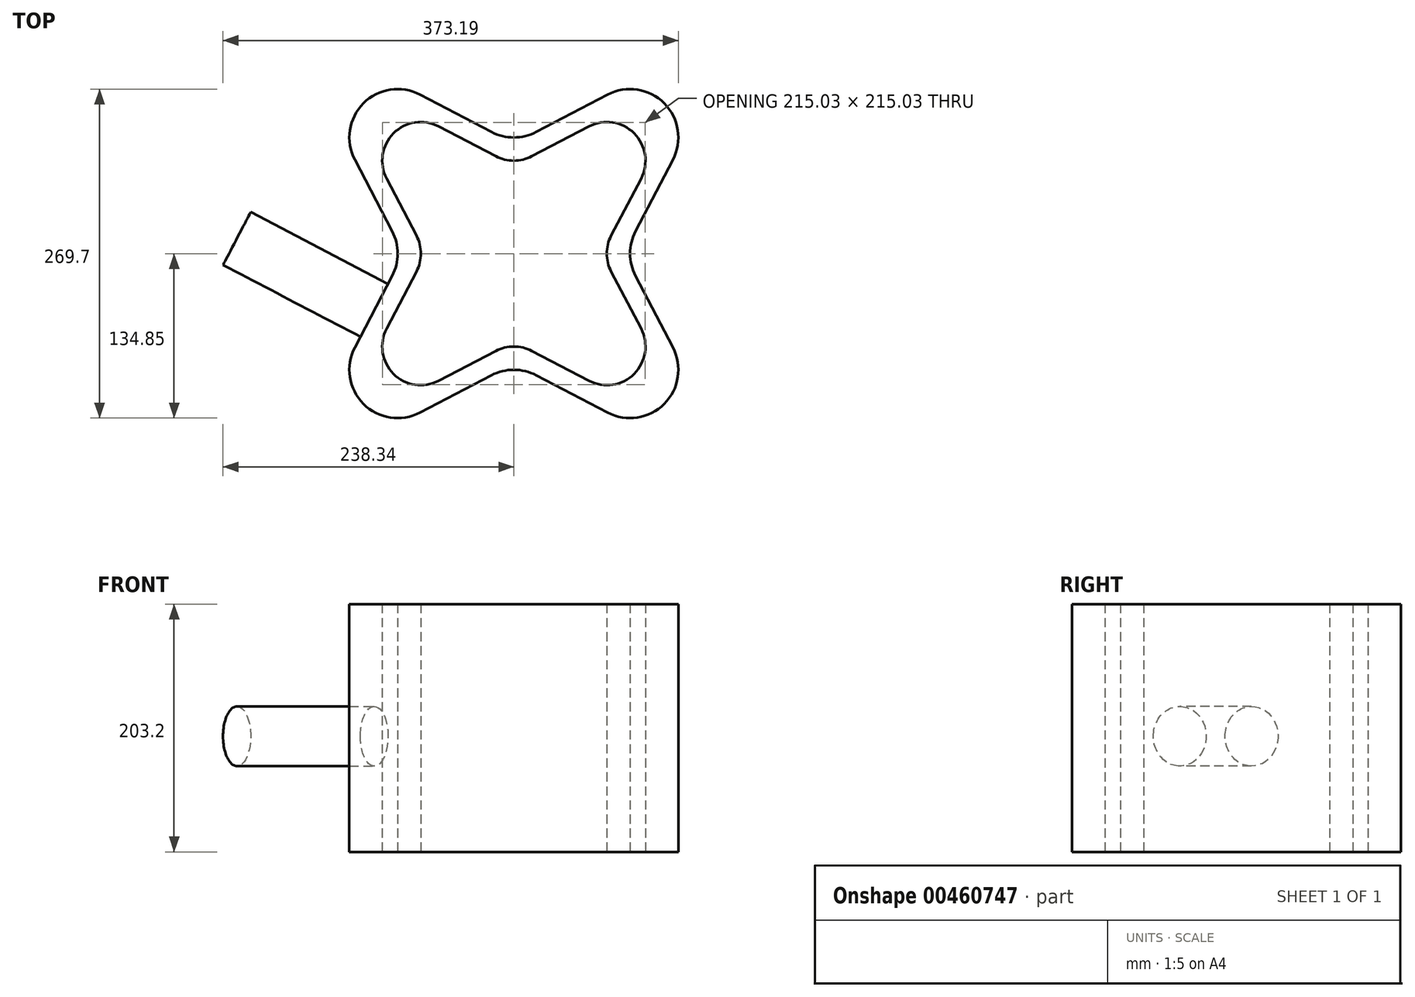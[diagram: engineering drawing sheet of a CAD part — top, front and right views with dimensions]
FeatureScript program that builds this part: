
annotation { "Feature Type Name" : "Feature", "Feature Type Description" : "" }
export const myFeature = defineFeature(function(context is Context, id is Id, definition is map)
    precondition{}
    {
        {
            var Q0;
            Q0=qCreatedBy(makeId("Top.planeOp"),FACE);
            var sketch = newSketch(context, id + "F0", { "sketchPlane" : qUnion([Q0])});
            skArc(sketch, "E0", {"start": v(-76.91, 130.35) * mm, "mid": v(-123.25, 123.25) * mm, "end": v(-130.35, 76.91) * mm});
            skArc(sketch, "E1", {"start": v(130.35, 76.91) * mm, "mid": v(123.25, 123.25) * mm, "end": v(76.91, 130.35) * mm});
            skArc(sketch, "E2", {"start": v(76.91, -130.35) * mm, "mid": v(123.25, -123.25) * mm, "end": v(130.35, -76.91) * mm});
            skArc(sketch, "E3", {"start": v(-130.35, -76.91) * mm, "mid": v(-123.25, -123.25) * mm, "end": v(-76.91, -130.35) * mm});
            skArc(sketch, "E4", {"start": v(18.34, -99.75) * mm, "mid": v(0, -95.25) * mm, "end": v(-18.34, -99.75) * mm});
            skArc(sketch, "E5", {"start": v(-18.34, 99.75) * mm, "mid": v(0, 95.25) * mm, "end": v(18.34, 99.75) * mm});
            skArc(sketch, "E6", {"start": v(-99.75, -18.34) * mm, "mid": v(-95.25, 0) * mm, "end": v(-99.75, 18.34) * mm});
            skArc(sketch, "E7", {"start": v(99.75, 18.34) * mm, "mid": v(95.25, 0) * mm, "end": v(99.75, -18.34) * mm});
            skLineSegment(sketch, "E8", {"start": v(-76.91, 130.35) * mm, "end": v(-18.34, 99.75) * mm});
            skLineSegment(sketch, "E9", {"start": v(18.34, 99.75) * mm, "end": v(76.91, 130.35) * mm});
            skLineSegment(sketch, "E10", {"start": v(130.35, 76.91) * mm, "end": v(99.75, 18.34) * mm});
            skLineSegment(sketch, "E11", {"start": v(99.75, -18.34) * mm, "end": v(130.35, -76.91) * mm});
            skLineSegment(sketch, "E12", {"start": v(76.91, -130.35) * mm, "end": v(18.34, -99.75) * mm});
            skLineSegment(sketch, "E13", {"start": v(-76.91, -130.35) * mm, "end": v(-18.34, -99.75) * mm});
            skLineSegment(sketch, "E14", {"start": v(-130.35, -76.91) * mm, "end": v(-99.75, -18.34) * mm});
            skLineSegment(sketch, "E15", {"start": v(-130.35, 76.91) * mm, "end": v(-99.75, 18.34) * mm});
            skLineSegment(sketch, "E16", {"start": v(-61.53, 104.28) * mm, "end": v(-14.67, 79.8) * mm});
            skLineSegment(sketch, "E17", {"start": v(14.67, 79.8) * mm, "end": v(61.53, 104.28) * mm});
            skLineSegment(sketch, "E18", {"start": v(61.53, -104.28) * mm, "end": v(14.67, -79.8) * mm});
            skLineSegment(sketch, "E19", {"start": v(-61.53, -104.28) * mm, "end": v(-14.67, -79.8) * mm});
            skLineSegment(sketch, "E20", {"start": v(-104.28, -61.53) * mm, "end": v(-79.8, -14.67) * mm});
            skLineSegment(sketch, "E21", {"start": v(-104.28, 61.53) * mm, "end": v(-79.8, 14.67) * mm});
            skArc(sketch, "E22", {"start": v(14.67, -79.8) * mm, "mid": v(0, -76.2) * mm, "end": v(-14.67, -79.8) * mm});
            skArc(sketch, "E23", {"start": v(-104.28, -61.53) * mm, "mid": v(-98.6, -98.6) * mm, "end": v(-61.53, -104.28) * mm});
            skArc(sketch, "E24", {"start": v(-79.8, -14.67) * mm, "mid": v(-76.2, 0) * mm, "end": v(-79.8, 14.67) * mm});
            skArc(sketch, "E25", {"start": v(-61.53, 104.28) * mm, "mid": v(-98.6, 98.6) * mm, "end": v(-104.28, 61.53) * mm});
            skArc(sketch, "E26", {"start": v(-14.67, 79.8) * mm, "mid": v(0, 76.2) * mm, "end": v(14.67, 79.8) * mm});
            skLineSegment(sketch, "E27", {"start": v(104.28, 61.53) * mm, "end": v(79.8, 14.67) * mm});
            skLineSegment(sketch, "E28", {"start": v(79.8, -14.67) * mm, "end": v(104.28, -61.53) * mm});
            skArc(sketch, "E29", {"start": v(61.53, -104.28) * mm, "mid": v(98.6, -98.6) * mm, "end": v(104.28, -61.53) * mm});
            skArc(sketch, "E30", {"start": v(104.28, 61.53) * mm, "mid": v(98.6, 98.6) * mm, "end": v(61.53, 104.28) * mm});
            skArc(sketch, "E31", {"start": v(79.8, 14.67) * mm, "mid": v(76.2, 0) * mm, "end": v(79.8, -14.67) * mm});
            skSolve(sketch);
        }
        {
            var Q0;
            Q0 = qSketchRegion(id + "F0", true);
            extrude(context, id + "F1", {"entities" : qUnion([Q0]), "depth" : 203.2 * mm});
        }
        {
            var Q0;
            Q0=makeQuery(id+"F1.opExtrude","SWEPT_FACE",FACE,{"disambiguationData":[OSD([sQuery(id+"F0.wireOp",EDGE,"E14")])]});
            var sketch = newSketch(context, id + "F2", { "sketchPlane" : qUnion([Q0])});
            skCircle(sketch, "E32", {"center": v(94.18, 94.8) * mm, "radius": 24.45 * mm});
            skSolve(sketch);
        }
        {
            var Q0;
            Q0 = qSketchRegion(id + "F2", true);
            extrude(context, id + "F3", {"entities" : qUnion([Q0]), "operationType" : NewBodyOperationType.ADD, "depth" : 127 * mm});
        }
        {
            var Q0;
            Q0=makeQuery(id+"F1.opExtrude","CAP_FACE",FACE,{"disambiguationData":[OSD([sQuery(id+"F0.wireOp",EDGE,"E0"),sQuery(id+"F0.wireOp",EDGE,"E1"),sQuery(id+"F0.wireOp",EDGE,"E2"),sQuery(id+"F0.wireOp",EDGE,"E3"),sQuery(id+"F0.wireOp",EDGE,"E4"),sQuery(id+"F0.wireOp",EDGE,"E5"),sQuery(id+"F0.wireOp",EDGE,"E6"),sQuery(id+"F0.wireOp",EDGE,"E7"),sQuery(id+"F0.wireOp",EDGE,"E8"),sQuery(id+"F0.wireOp",EDGE,"E9"),sQuery(id+"F0.wireOp",EDGE,"E10"),sQuery(id+"F0.wireOp",EDGE,"E11"),sQuery(id+"F0.wireOp",EDGE,"E12"),sQuery(id+"F0.wireOp",EDGE,"E13"),sQuery(id+"F0.wireOp",EDGE,"E14"),sQuery(id+"F0.wireOp",EDGE,"E15"),sQuery(id+"F0.wireOp",EDGE,"E16"),sQuery(id+"F0.wireOp",EDGE,"E17"),sQuery(id+"F0.wireOp",EDGE,"E18"),sQuery(id+"F0.wireOp",EDGE,"E19"),sQuery(id+"F0.wireOp",EDGE,"E20"),sQuery(id+"F0.wireOp",EDGE,"E21"),sQuery(id+"F0.wireOp",EDGE,"E22"),sQuery(id+"F0.wireOp",EDGE,"E23"),sQuery(id+"F0.wireOp",EDGE,"E24"),sQuery(id+"F0.wireOp",EDGE,"E25"),sQuery(id+"F0.wireOp",EDGE,"E26"),sQuery(id+"F0.wireOp",EDGE,"E27"),sQuery(id+"F0.wireOp",EDGE,"E28"),sQuery(id+"F0.wireOp",EDGE,"E29"),sQuery(id+"F0.wireOp",EDGE,"E30"),sQuery(id+"F0.wireOp",EDGE,"E31")])],"isStart":true});
            var sketch = newSketch(context, id + "F4", { "sketchPlane" : qUnion([Q0])});
            skEllipse(sketch, "E33", {"center": v(106.77, 112.27) * mm, "majorRadius": 38.37 * mm, "minorRadius": 11.53 * mm, "majorAxis": v(-0.7, -0.72)});
            skSolve(sketch);
        }
        {
            var Q0;
            Q0=sQuery(id+"F4.wireOp",EDGE,"E33");
            extrude(context, id + "F5", {"bodyType" : ToolBodyType.SURFACE, "surfaceEntities" : qUnion([Q0]), "endBound" : BoundingType.SYMMETRIC, "depth" : 381 * mm});
        }
    });
